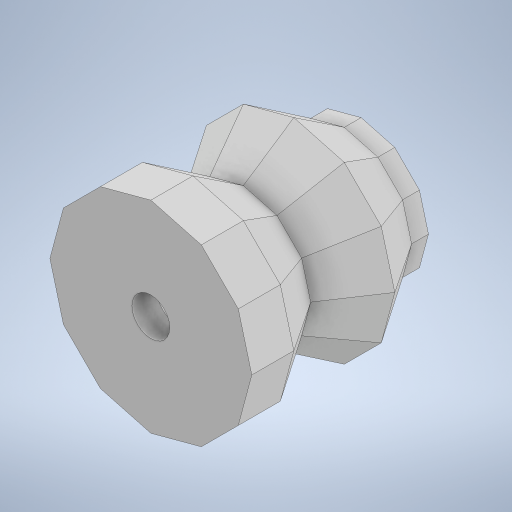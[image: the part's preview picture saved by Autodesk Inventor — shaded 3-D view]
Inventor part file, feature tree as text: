
AUTODESK INVENTOR PART (.ipt)
format: ipt  version: 2023 (Build 270158000, 158)  size: 355,328 bytes
history: native  units: in
note: dims shown in document units (in); Inventor stores cm internally (conversion verified against a paired STEP export)
features: sketch x6, extrude x4, projected_geometry x3, other x2, mirror x2, loft x1, shell x1
ambient origin geometry x8: Origin, YZ Plane, XZ Plane, XY Plane, X Axis, Y Axis, Z Axis, Center Point
bodies: Body1 (feature_tree)
feature tree (19):
  other  "솔리드1"
  sketch  "스케치1"
  other  "작업 평면1"
  loft  "로프트1"
  mirror  "미러1"
  mirror  "미러2"
  extrude  "돌출1"  Depth=0.2362in
  shell  "쉘1"  Thickness=0.6299in
  extrude  "돌출2"  TaperAngle=0.0deg  [1 undecoded]
  extrude  "돌출3"  TaperAngle=0.0deg  [1 undecoded]
  extrude  "돌출4"  Depth=0.0984in TaperAngle=0.0deg
  sketch  "스케치2"
  sketch  "스케치3"
  projected_geometry  "투영된 루프1"
  sketch  "스케치4"
  projected_geometry  "투영된 루프2"
  sketch  "스케치5"
  sketch  "스케치6"
  projected_geometry  "투영된 루프3"
note: 2 required parameter values undecoded (feature->parameter linkage not recoverable at this tier; creation-order binding heuristic only, values carry confidence <= 0.55)
